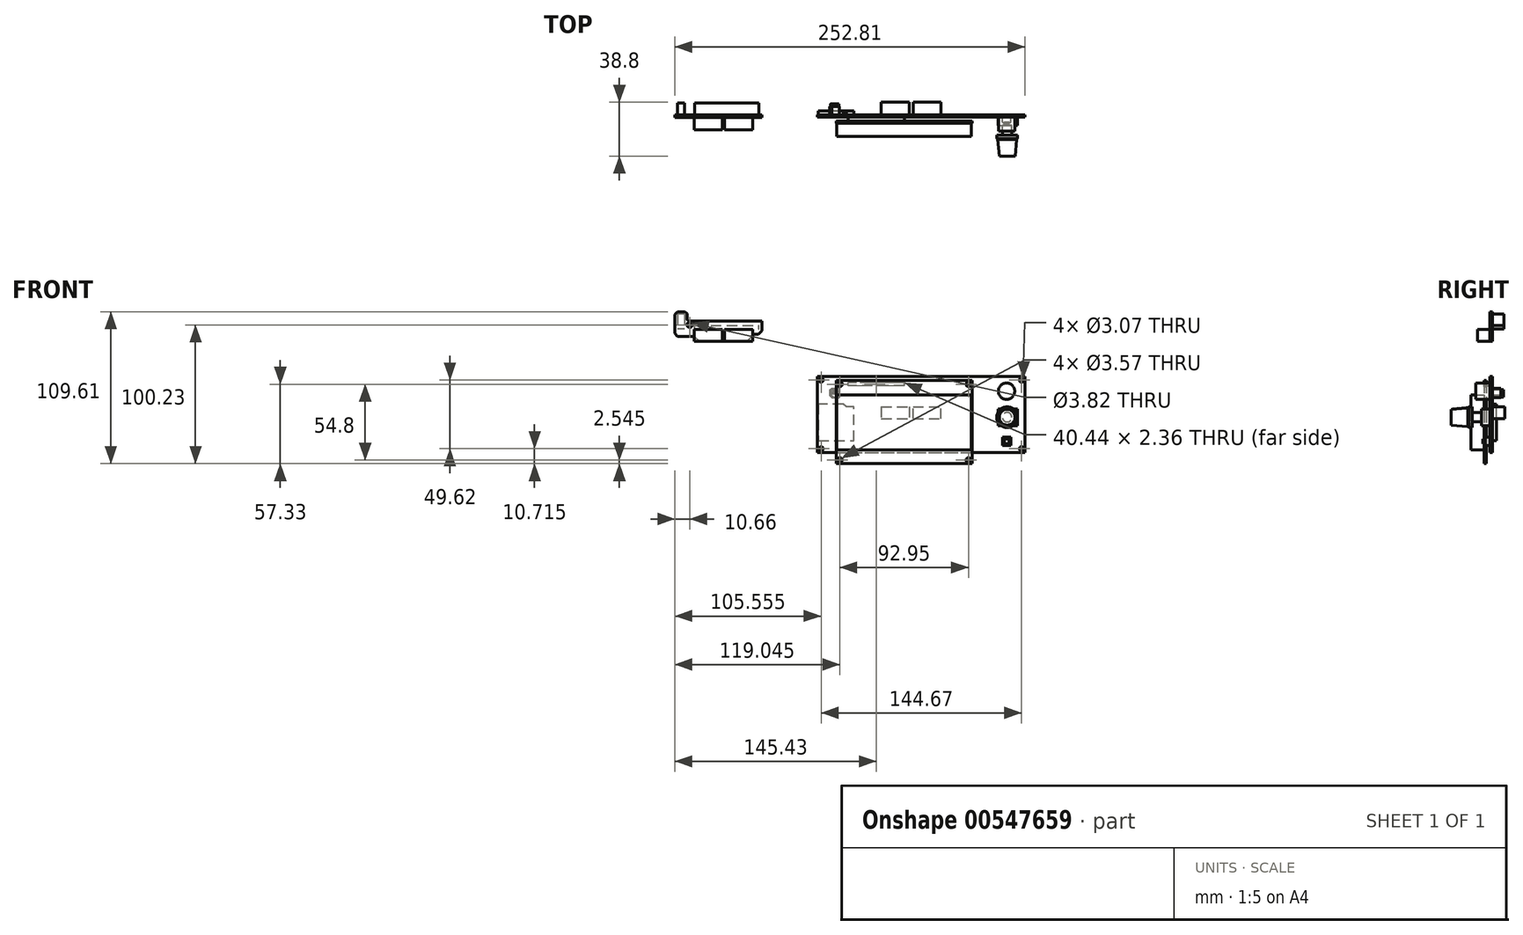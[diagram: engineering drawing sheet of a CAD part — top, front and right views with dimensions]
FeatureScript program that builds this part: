
annotation { "Feature Type Name" : "Feature", "Feature Type Description" : "" }
export const myFeature = defineFeature(function(context is Context, id is Id, definition is map)
    precondition{}
    {
        {
            var Q0;
            Q0=qCreatedBy(makeId("Front.planeOp"),FACE);
            var sketch = newSketch(context, id + "F0", { "sketchPlane" : qUnion([Q0])});
            skLineSegment(sketch, "E0.bottom", {"start": v(0, 0) * mm, "end": v(150.07, 0) * mm});
            skLineSegment(sketch, "E0.top", {"start": v(0, -55.1) * mm, "end": v(150.07, -55.1) * mm});
            skLineSegment(sketch, "E0.left", {"start": v(0, 0) * mm, "end": v(0, -55.1) * mm});
            skLineSegment(sketch, "E0.right", {"start": v(150.07, 0) * mm, "end": v(150.07, -55.1) * mm});
            skLineSegment(sketch, "E1", {"start": v(0, -2.7) * mm, "end": v(150.07, -2.7) * mm, "construction": true});
            skLineSegment(sketch, "E2", {"start": v(0, -52.33) * mm, "end": v(150.07, -52.32) * mm, "construction": true});
            skLineSegment(sketch, "E3", {"start": v(2.81, 0) * mm, "end": v(2.82, -55.1) * mm, "construction": true});
            skLineSegment(sketch, "E4", {"start": v(147.49, 0) * mm, "end": v(147.49, -55.1) * mm, "construction": true});
            skCircle(sketch, "E5", {"center": v(2.81, -2.7) * mm, "radius": 1.53 * mm});
            skCircle(sketch, "E6", {"center": v(2.81, -52.33) * mm, "radius": 1.53 * mm});
            skCircle(sketch, "E7", {"center": v(147.49, -2.7) * mm, "radius": 1.53 * mm});
            skCircle(sketch, "E8", {"center": v(147.49, -52.32) * mm, "radius": 1.53 * mm});
            skSolve(sketch);
        }
        {
            var Q0;
            Q0=qSketchRegion(id+"F0",true);
            extrude(context, id + "F1", {"entities" : qUnion([Q0]), "depth" : 1.63 * mm});
        }
        {
            var Q0;
            Q0=makeQuery(id+"F1.opExtrude","CAP_FACE",FACE,{"disambiguationData":[OSD([sQuery(id+"F0.wireOp",EDGE,"E0.bottom"),sQuery(id+"F0.wireOp",EDGE,"E0.top"),sQuery(id+"F0.wireOp",EDGE,"E0.left"),sQuery(id+"F0.wireOp",EDGE,"E0.right")])],"isStart":false});
            cPlane(context, id + "F2", {"entities" : qUnion([Q0]), "cplaneType" : CPlaneType.OFFSET, "offset" : 2.7 * mm, "width" : 150 * mm, "height" : 150 * mm});
        }
        {
            var Q0;
            Q0=qCreatedBy(id+"F2.planeOp",FACE);
            var sketch = newSketch(context, id + "F3", { "sketchPlane" : qUnion([Q0])});
            skLineSegment(sketch, "E9.bottom", {"start": v(13.62, -3.08) * mm, "end": v(111.77, -3.08) * mm});
            skLineSegment(sketch, "E9.top", {"start": v(13.62, -63.04) * mm, "end": v(111.77, -63.04) * mm});
            skLineSegment(sketch, "E9.left", {"start": v(13.62, -3.08) * mm, "end": v(13.62, -63.04) * mm});
            skLineSegment(sketch, "E9.right", {"start": v(111.77, -3.08) * mm, "end": v(111.77, -63.04) * mm});
            skLineSegment(sketch, "E10.bottom", {"start": v(16.3, -5.7) * mm, "end": v(109.26, -5.7) * mm, "construction": true});
            skLineSegment(sketch, "E10.top", {"start": v(16.3, -60.5) * mm, "end": v(109.26, -60.5) * mm, "construction": true});
            skLineSegment(sketch, "E10.left", {"start": v(16.3, -5.7) * mm, "end": v(16.3, -60.5) * mm, "construction": true});
            skLineSegment(sketch, "E10.right", {"start": v(109.26, -5.7) * mm, "end": v(109.26, -60.5) * mm, "construction": true});
            skCircle(sketch, "E11", {"center": v(16.3, -5.7) * mm, "radius": 1.78 * mm});
            skCircle(sketch, "E12", {"center": v(109.26, -5.7) * mm, "radius": 1.78 * mm});
            skCircle(sketch, "E13", {"center": v(16.3, -60.5) * mm, "radius": 1.78 * mm});
            skCircle(sketch, "E14", {"center": v(109.26, -60.5) * mm, "radius": 1.78 * mm});
            skSolve(sketch);
        }
        {
            var Q0;
            Q0=qSketchRegion(id+"F3",true);
            extrude(context, id + "F4", {"entities" : qUnion([Q0]), "depth" : 1.62 * mm});
        }
        {
            var Q0;
            Q0=makeQuery(id+"F4.opExtrude","CAP_FACE",FACE,{"disambiguationData":[OSD([sQuery(id+"F3.wireOp",EDGE,"E9.bottom"),sQuery(id+"F3.wireOp",EDGE,"E9.top"),sQuery(id+"F3.wireOp",EDGE,"E9.left"),sQuery(id+"F3.wireOp",EDGE,"E9.right")])],"isStart":false});
            var sketch = newSketch(context, id + "F5", { "sketchPlane" : qUnion([Q0])});
            skLineSegment(sketch, "E15", {"start": v(62.7, -3.08) * mm, "end": v(62.7, -63.04) * mm, "construction": true});
            skLineSegment(sketch, "E16.bottom", {"start": v(14.18, -13.36) * mm, "end": v(111.2, -13.36) * mm});
            skLineSegment(sketch, "E16.top", {"start": v(14.19, -53.18) * mm, "end": v(111.2, -53.18) * mm});
            skLineSegment(sketch, "E16.left", {"start": v(14.19, -13.36) * mm, "end": v(14.19, -53.18) * mm});
            skLineSegment(sketch, "E16.right", {"start": v(111.2, -13.36) * mm, "end": v(111.2, -53.18) * mm});
            skCircle(sketch, "E17", {"center": v(62.7, -33.06) * mm, "radius": 48.5 * mm, "construction": true});
            skSolve(sketch);
        }
        {
            var Q0;
            Q0=qSketchRegion(id+"F5",true);
            extrude(context, id + "F6", {"entities" : qUnion([Q0]), "operationType" : NewBodyOperationType.ADD, "depth" : 9.45 * mm});
        }
        {
            var Q0;
            Q0=makeQuery(id+"F1.opExtrude","CAP_FACE",FACE,{"disambiguationData":[OSD([sQuery(id+"F0.wireOp",EDGE,"E0.bottom"),sQuery(id+"F0.wireOp",EDGE,"E0.top"),sQuery(id+"F0.wireOp",EDGE,"E0.left"),sQuery(id+"F0.wireOp",EDGE,"E0.right")])],"isStart":false});
            var sketch = newSketch(context, id + "F7", { "sketchPlane" : qUnion([Q0])});
            skLineSegment(sketch, "E18.bottom", {"start": v(133.8, -43.96) * mm, "end": v(139.76, -43.96) * mm});
            skLineSegment(sketch, "E18.top", {"start": v(133.8, -49.92) * mm, "end": v(139.76, -49.92) * mm});
            skLineSegment(sketch, "E18.left", {"start": v(133.8, -43.96) * mm, "end": v(133.8, -49.92) * mm});
            skLineSegment(sketch, "E18.right", {"start": v(139.76, -43.96) * mm, "end": v(139.76, -49.92) * mm});
            skCircle(sketch, "E19", {"center": v(136.78, -46.94) * mm, "radius": 2.98 * mm, "construction": true});
            skSolve(sketch);
        }
        {
            var Q0;
            Q0=qSketchRegion(id+"F7",true);
            extrude(context, id + "F8", {"entities" : qUnion([Q0]), "operationType" : NewBodyOperationType.ADD, "depth" : 3.55 * mm});
        }
        {
            var Q0;
            Q0=makeQuery(id+"F8.opExtrude","CAP_FACE",FACE,{"disambiguationData":[OSD([sQuery(id+"F7.wireOp",EDGE,"E18.bottom"),sQuery(id+"F7.wireOp",EDGE,"E18.top"),sQuery(id+"F7.wireOp",EDGE,"E18.left"),sQuery(id+"F7.wireOp",EDGE,"E18.right")])],"isStart":false});
            var sketch = newSketch(context, id + "F9", { "sketchPlane" : qUnion([Q0])});
            skLineSegment(sketch, "E20", {"start": v(133.8, -43.96) * mm, "end": v(139.76, -49.92) * mm, "construction": true});
            skCircle(sketch, "E21", {"center": v(136.78, -46.94) * mm, "radius": 1.76 * mm});
            skSolve(sketch);
        }
        {
            var Q0;
            Q0=qSketchRegion(id+"F9",true);
            extrude(context, id + "F10", {"entities" : qUnion([Q0]), "operationType" : NewBodyOperationType.ADD, "depth" : 1.57 * mm});
        }
        {
            var Q0;
            Q0=makeQuery(id+"F1.opExtrude","CAP_FACE",FACE,{"disambiguationData":[OSD([sQuery(id+"F0.wireOp",EDGE,"E0.bottom"),sQuery(id+"F0.wireOp",EDGE,"E0.top"),sQuery(id+"F0.wireOp",EDGE,"E0.left"),sQuery(id+"F0.wireOp",EDGE,"E0.right"),sQuery(id+"F0.wireOp",EDGE,"E5"),sQuery(id+"F0.wireOp",EDGE,"E6"),sQuery(id+"F0.wireOp",EDGE,"E7"),sQuery(id+"F0.wireOp",EDGE,"E8")])],"isStart":false});
            var sketch = newSketch(context, id + "F11", { "sketchPlane" : qUnion([Q0])});
            skLineSegment(sketch, "E22.bottom", {"start": v(130.73, -23.6) * mm, "end": v(144.54, -23.6) * mm});
            skLineSegment(sketch, "E22.top", {"start": v(130.73, -35.51) * mm, "end": v(144.54, -35.51) * mm});
            skLineSegment(sketch, "E22.left", {"start": v(130.73, -23.6) * mm, "end": v(130.73, -35.51) * mm});
            skLineSegment(sketch, "E22.right", {"start": v(144.54, -23.6) * mm, "end": v(144.54, -35.51) * mm});
            skSolve(sketch);
        }
        {
            var Q0;
            Q0=qSketchRegion(id+"F11",true);
            extrude(context, id + "F12", {"entities" : qUnion([Q0]), "operationType" : NewBodyOperationType.ADD, "depth" : 6.04 * mm});
        }
        {
            var Q0;
            Q0=makeQuery(id+"F12.opExtrude","CAP_FACE",FACE,{"disambiguationData":[OSD([sQuery(id+"F11.wireOp",EDGE,"E22.bottom"),sQuery(id+"F11.wireOp",EDGE,"E22.top"),sQuery(id+"F11.wireOp",EDGE,"E22.left"),sQuery(id+"F11.wireOp",EDGE,"E22.right")])],"isStart":false});
            var sketch = newSketch(context, id + "F13", { "sketchPlane" : qUnion([Q0])});
            skLineSegment(sketch, "E23", {"start": v(130.73, -29.55) * mm, "end": v(144.54, -29.55) * mm, "construction": true});
            skCircle(sketch, "E24", {"center": v(137.11, -29.55) * mm, "radius": 3.41 * mm});
            skSolve(sketch);
        }
        {
            var Q0;
            Q0=qSketchRegion(id+"F13",true);
            extrude(context, id + "F14", {"entities" : qUnion([Q0]), "operationType" : NewBodyOperationType.ADD, "depth" : 6.86 * mm});
        }
        {
            var Q0;
            Q0=sQuery(id+"F13.wireOp",EDGE,"E23");
            cPoint(context, id + "F15", {"entities" : qUnion([Q0]), "parameter" : 0.5});
        }
        {
            var Q0;
            Q0=qCreatedBy(makeId("Top.planeOp"),FACE);
            var Q1;
            Q1=qCreatedBy(id+"F15",VERTEX);
            cPlane(context, id + "F16", {"entities" : qUnion([Q0, Q1]), "cplaneType" : CPlaneType.PLANE_POINT, "offset" : 25 * mm, "width" : 150 * mm, "height" : 150 * mm});
        }
        {
            var Q0;
            Q0=qCreatedBy(id+"F16.planeOp",FACE);
            var sketch = newSketch(context, id + "F17", { "sketchPlane" : qUnion([Q0])});
            skLineSegment(sketch, "E25.0", {"start": v(140.52, -14.53) * mm, "end": v(133.7, -14.53) * mm, "construction": true});
            skLineSegment(sketch, "E26", {"start": v(137.11, -14.53) * mm, "end": v(137.11, -29.65) * mm});
            skLineSegment(sketch, "E27", {"start": v(137.11, -29.65) * mm, "end": v(142.84, -29.65) * mm});
            skLineSegment(sketch, "E28", {"start": v(142.84, -29.65) * mm, "end": v(143.96, -17.58) * mm});
            skLineSegment(sketch, "E29", {"start": v(143.96, -17.58) * mm, "end": v(144.6, -16.95) * mm});
            skLineSegment(sketch, "E30", {"start": v(144.6, -16.95) * mm, "end": v(144.6, -14.53) * mm});
            skLineSegment(sketch, "E31", {"start": v(144.6, -14.53) * mm, "end": v(137.11, -14.53) * mm});
            skSolve(sketch);
        }
        {
            var Q0;
            Q0=qSketchRegion(id+"F17",true);
            var Q1;
            Q1=sQuery(id+"F17.wireOp",EDGE,"E26");
            revolve(context, id + "F18", {"operationType" : NewBodyOperationType.ADD, "entities" : qUnion([Q0]), "axis" : qUnion([Q1]), "revolveType" : RevolveType.FULL});
        }
        {
            var Q0;
            Q0=makeQuery(id+"F1.opExtrude","CAP_FACE",FACE,{"disambiguationData":[OSD([sQuery(id+"F0.wireOp",EDGE,"E0.bottom"),sQuery(id+"F0.wireOp",EDGE,"E0.top"),sQuery(id+"F0.wireOp",EDGE,"E0.left"),sQuery(id+"F0.wireOp",EDGE,"E0.right"),sQuery(id+"F0.wireOp",EDGE,"E5"),sQuery(id+"F0.wireOp",EDGE,"E6"),sQuery(id+"F0.wireOp",EDGE,"E7"),sQuery(id+"F0.wireOp",EDGE,"E8")])],"isStart":false});
            var sketch = newSketch(context, id + "F19", { "sketchPlane" : qUnion([Q0])});
            skCircle(sketch, "E32", {"center": v(136.68, -10.73) * mm, "radius": 5.9 * mm});
            skSolve(sketch);
        }
        {
            var Q0;
            Q0=qSketchRegion(id+"F19",true);
            extrude(context, id + "F20", {"entities" : qUnion([Q0]), "operationType" : NewBodyOperationType.ADD, "depth" : 10.15 * mm});
        }
        {
            var Q0;
            Q0=makeQuery(id+"F1.opExtrude","CAP_FACE",FACE,{"disambiguationData":[OSD([sQuery(id+"F0.wireOp",EDGE,"E0.bottom"),sQuery(id+"F0.wireOp",EDGE,"E0.top"),sQuery(id+"F0.wireOp",EDGE,"E0.left"),sQuery(id+"F0.wireOp",EDGE,"E0.right"),sQuery(id+"F0.wireOp",EDGE,"E5"),sQuery(id+"F0.wireOp",EDGE,"E6"),sQuery(id+"F0.wireOp",EDGE,"E7"),sQuery(id+"F0.wireOp",EDGE,"E8")])],"isStart":true});
            var sketch = newSketch(context, id + "F21", { "sketchPlane" : qUnion([Q0])});
            skLineSegment(sketch, "E33", {"start": v(-0.8, -46.57) * mm, "end": v(-26.48, -46.57) * mm});
            skLineSegment(sketch, "E34", {"start": v(-26.48, -46.57) * mm, "end": v(-26.48, -22.15) * mm});
            skLineSegment(sketch, "E35", {"start": v(-26.48, -22.15) * mm, "end": v(-21.02, -22.15) * mm});
            skLineSegment(sketch, "E36", {"start": v(-21.02, -22.15) * mm, "end": v(-18.87, -20) * mm});
            skLineSegment(sketch, "E37", {"start": v(-18.87, -20) * mm, "end": v(-0.8, -20) * mm});
            skLineSegment(sketch, "E38", {"start": v(-0.8, -20) * mm, "end": v(-0.8, -46.57) * mm});
            skSolve(sketch);
        }
        {
            var Q0;
            Q0=qSketchRegion(id+"F21",true);
            extrude(context, id + "F22", {"entities" : qUnion([Q0]), "operationType" : NewBodyOperationType.ADD, "depth" : 2.91 * mm});
        }
        {
            var Q0;
            Q0=makeQuery(id+"F1.opExtrude","CAP_FACE",FACE,{"disambiguationData":[OSD([sQuery(id+"F0.wireOp",EDGE,"E0.bottom"),sQuery(id+"F0.wireOp",EDGE,"E0.top"),sQuery(id+"F0.wireOp",EDGE,"E0.left"),sQuery(id+"F0.wireOp",EDGE,"E0.right"),sQuery(id+"F0.wireOp",EDGE,"E5"),sQuery(id+"F0.wireOp",EDGE,"E6"),sQuery(id+"F0.wireOp",EDGE,"E7"),sQuery(id+"F0.wireOp",EDGE,"E8")])],"isStart":true});
            var sketch = newSketch(context, id + "F23", { "sketchPlane" : qUnion([Q0])});
            skLineSegment(sketch, "E39", {"start": v(-15.96, -11.92) * mm, "end": v(-9.02, -11.92) * mm, "construction": true});
            skLineSegment(sketch, "E40", {"start": v(-9.02, -11.92) * mm, "end": v(-9.02, -10.05) * mm});
            skLineSegment(sketch, "E41", {"start": v(-9.02, -10.05) * mm, "end": v(-10.48, -8.6) * mm});
            skLineSegment(sketch, "E42", {"start": v(-10.48, -8.6) * mm, "end": v(-15.96, -8.6) * mm});
            skLineSegment(sketch, "E43", {"start": v(-15.96, -8.6) * mm, "end": v(-15.96, -11.92) * mm});
            skLineSegment(sketch, "E44.MirrorCS", {"start": v(-15.96, -15.25) * mm, "end": v(-15.96, -11.92) * mm});
            skLineSegment(sketch, "E45.MirrorCS", {"start": v(-10.48, -15.25) * mm, "end": v(-15.96, -15.25) * mm});
            skLineSegment(sketch, "E46.MirrorCS", {"start": v(-9.02, -13.78) * mm, "end": v(-10.49, -15.25) * mm});
            skLineSegment(sketch, "E47.MirrorCS", {"start": v(-9.02, -11.92) * mm, "end": v(-9.02, -13.78) * mm});
            skSolve(sketch);
        }
        {
            var Q0;
            Q0=qSketchRegion(id+"F23",true);
            extrude(context, id + "F24", {"entities" : qUnion([Q0]), "operationType" : NewBodyOperationType.ADD, "depth" : 6.15 * mm});
        }
        {
            var Q0;
            Q0=makeQuery(id+"F24.opExtrude","CAP_FACE",FACE,{"disambiguationData":[OSD([sQuery(id+"F23.wireOp",EDGE,"E40"),sQuery(id+"F23.wireOp",EDGE,"E41"),sQuery(id+"F23.wireOp",EDGE,"E42"),sQuery(id+"F23.wireOp",EDGE,"E43"),sQuery(id+"F23.wireOp",EDGE,"E44.MirrorCS"),sQuery(id+"F23.wireOp",EDGE,"E45.MirrorCS"),sQuery(id+"F23.wireOp",EDGE,"E46.MirrorCS"),sQuery(id+"F23.wireOp",EDGE,"E47.MirrorCS")])],"isStart":false});
            var sketch = newSketch(context, id + "F25", { "sketchPlane" : qUnion([Q0])});
            skLineSegment(sketch, "E48.0", {"start": v(-15.96, -11.92) * mm, "end": v(-9.02, -11.92) * mm, "construction": true});
            skCircle(sketch, "E49", {"center": v(-12.5, -11.92) * mm, "radius": 3 * mm});
            skLineSegment(sketch, "E50.bottom", {"start": v(-14.72, -11.4) * mm, "end": v(-12.5, -11.4) * mm});
            skLineSegment(sketch, "E50.left", {"start": v(-14.72, -11.4) * mm, "end": v(-14.72, -11.92) * mm});
            skLineSegment(sketch, "E51", {"start": v(-12.5, -11.92) * mm, "end": v(-12.5, -8.91) * mm, "construction": true});
            skLineSegment(sketch, "E52", {"start": v(-12.5, -11.92) * mm, "end": v(-12.5, -14.93) * mm, "construction": true});
            skLineSegment(sketch, "E53", {"start": v(-14.25, -9.48) * mm, "end": v(-13.82, -9.48) * mm});
            skLineSegment(sketch, "E54", {"start": v(-13.82, -9.48) * mm, "end": v(-13.82, -10.03) * mm});
            skLineSegment(sketch, "E55", {"start": v(-13.82, -10.03) * mm, "end": v(-12.5, -10.03) * mm});
            skLineSegment(sketch, "E56.MirrorCS", {"start": v(-14.72, -12.45) * mm, "end": v(-12.5, -12.45) * mm});
            skLineSegment(sketch, "E57.MirrorCS", {"start": v(-14.72, -12.45) * mm, "end": v(-14.72, -11.92) * mm});
            skLineSegment(sketch, "E58.MirrorCS", {"start": v(-11.16, -10.03) * mm, "end": v(-12.5, -10.03) * mm});
            skLineSegment(sketch, "E59.MirrorCS", {"start": v(-11.16, -9.48) * mm, "end": v(-11.16, -10.03) * mm});
            skLineSegment(sketch, "E60.MirrorCS", {"start": v(-10.73, -9.48) * mm, "end": v(-11.16, -9.48) * mm});
            skLineSegment(sketch, "E61.MirrorCS", {"start": v(-10.27, -11.4) * mm, "end": v(-12.5, -11.4) * mm});
            skLineSegment(sketch, "E62.MirrorCS", {"start": v(-10.27, -11.4) * mm, "end": v(-10.27, -11.92) * mm});
            skLineSegment(sketch, "E63.MirrorCS", {"start": v(-10.27, -12.45) * mm, "end": v(-10.27, -11.92) * mm});
            skLineSegment(sketch, "E64.MirrorCS", {"start": v(-10.27, -12.45) * mm, "end": v(-12.5, -12.45) * mm});
            skSolve(sketch);
        }
        {
            var Q0;
            Q0=makeQuery(id+"F25.imprint","IMPRINT",FACE,{"disambiguationData":[TD([[makeQuery(id+"F25.imprint","IMPRINT",EDGE,{"derivedFrom":sQuery(id+"F25.wireOp",EDGE,"E50.bottom")}),1.0]])]});
            extrude(context, id + "F26", {"entities" : qUnion([Q0]), "operationType" : NewBodyOperationType.ADD, "depth" : 1.85 * mm});
        }
        {
            var Q0;
            Q0=makeQuery(id+"F1.opExtrude","CAP_FACE",FACE,{"disambiguationData":[OSD([sQuery(id+"F0.wireOp",EDGE,"E0.bottom"),sQuery(id+"F0.wireOp",EDGE,"E0.top"),sQuery(id+"F0.wireOp",EDGE,"E0.left"),sQuery(id+"F0.wireOp",EDGE,"E0.right"),sQuery(id+"F0.wireOp",EDGE,"E5"),sQuery(id+"F0.wireOp",EDGE,"E6"),sQuery(id+"F0.wireOp",EDGE,"E7"),sQuery(id+"F0.wireOp",EDGE,"E8")])],"isStart":true});
            var sketch = newSketch(context, id + "F27", { "sketchPlane" : qUnion([Q0])});
            skLineSegment(sketch, "E65.bottom", {"start": v(-46.17, -22) * mm, "end": v(-66.44, -22) * mm});
            skLineSegment(sketch, "E65.top", {"start": v(-46.17, -30.71) * mm, "end": v(-66.44, -30.71) * mm});
            skLineSegment(sketch, "E65.left", {"start": v(-46.17, -22) * mm, "end": v(-46.17, -30.71) * mm});
            skLineSegment(sketch, "E65.right", {"start": v(-66.44, -22) * mm, "end": v(-66.44, -30.71) * mm});
            skLineSegment(sketch, "E66.bottom", {"start": v(-69.19, -30.71) * mm, "end": v(-89.46, -30.71) * mm});
            skLineSegment(sketch, "E66.top", {"start": v(-69.19, -22) * mm, "end": v(-89.46, -22) * mm});
            skLineSegment(sketch, "E66.left", {"start": v(-69.19, -30.71) * mm, "end": v(-69.19, -22) * mm});
            skLineSegment(sketch, "E66.right", {"start": v(-89.46, -30.71) * mm, "end": v(-89.46, -22) * mm});
            skLineSegment(sketch, "E67", {"start": v(-69.19, -30.71) * mm, "end": v(-66.44, -30.71) * mm, "construction": true});
            skLineSegment(sketch, "E68", {"start": v(-66.44, -22) * mm, "end": v(-69.19, -22) * mm, "construction": true});
            skSolve(sketch);
        }
        {
            var Q0;
            Q0=qSketchRegion(id+"F27",true);
            extrude(context, id + "F28", {"entities" : qUnion([Q0]), "operationType" : NewBodyOperationType.ADD, "depth" : 9.15 * mm});
        }
        {
            var Q0;
            Q0=qCreatedBy(makeId("Front.planeOp"),FACE);
            var sketch = newSketch(context, id + "F29", { "sketchPlane" : qUnion([Q0])});
            skLineSegment(sketch, "E69", {"start": v(-40, 40) * mm, "end": v(-92.4, 40) * mm});
            skLineSegment(sketch, "E70", {"start": v(-93.99, 41.6) * mm, "end": v(-93.99, 45.24) * mm});
            skLineSegment(sketch, "E71", {"start": v(-93.99, 45.24) * mm, "end": v(-95.32, 46.57) * mm});
            skLineSegment(sketch, "E72", {"start": v(-95.32, 46.57) * mm, "end": v(-100.78, 46.57) * mm});
            skLineSegment(sketch, "E73", {"start": v(-100.78, 46.57) * mm, "end": v(-102.74, 44.6) * mm});
            skLineSegment(sketch, "E74", {"start": v(-102.74, 44.6) * mm, "end": v(-102.74, 30.85) * mm});
            skLineSegment(sketch, "E75", {"start": v(-102.74, 30.85) * mm, "end": v(-100.78, 28.89) * mm});
            skLineSegment(sketch, "E76", {"start": v(-100.78, 28.89) * mm, "end": v(-88.78, 28.89) * mm});
            skLineSegment(sketch, "E77", {"start": v(-88.78, 28.89) * mm, "end": v(-85.05, 25.16) * mm});
            skLineSegment(sketch, "E78", {"start": v(-85.05, 25.16) * mm, "end": v(-50.73, 25.16) * mm});
            skLineSegment(sketch, "E79", {"start": v(-50.73, 25.16) * mm, "end": v(-45.51, 30.38) * mm});
            skLineSegment(sketch, "E80", {"start": v(-42.42, 30.38) * mm, "end": v(-40, 32.8) * mm});
            skLineSegment(sketch, "E81", {"start": v(-40, 32.8) * mm, "end": v(-40, 40) * mm});
            skLineSegment(sketch, "E82", {"start": v(-45.51, 30.38) * mm, "end": v(-42.42, 30.38) * mm});
            skLineSegment(sketch, "E83", {"start": v(-100.78, 46.57) * mm, "end": v(-100.78, 28.89) * mm, "construction": true});
            skPoint(sketch, "E84.visualSharp", {"position": v(-93.99, 40) * mm});
            skArc(sketch, "E84.filletArc", {"start": v(-94, 41.6) * mm, "mid": v(-93.52, 40.47) * mm, "end": v(-92.4, 40) * mm});
            skCircle(sketch, "E85", {"center": v(-92.08, 37.19) * mm, "radius": 1.91 * mm});
            skLineSegment(sketch, "E86", {"start": v(-93.99, 41.6) * mm, "end": v(-93.99, 28.89) * mm, "construction": true});
            skSolve(sketch);
        }
        {
            var Q0;
            Q0=qSketchRegion(id+"F29",true);
            extrude(context, id + "F30", {"entities" : qUnion([Q0]), "depth" : 1.74 * mm});
        }
        {
            var Q0;
            Q0=makeQuery(id+"F30.opExtrude","CAP_FACE",FACE,{"disambiguationData":[OSD([sQuery(id+"F29.wireOp",EDGE,"E69"),sQuery(id+"F29.wireOp",EDGE,"E70"),sQuery(id+"F29.wireOp",EDGE,"E71"),sQuery(id+"F29.wireOp",EDGE,"E72"),sQuery(id+"F29.wireOp",EDGE,"E73"),sQuery(id+"F29.wireOp",EDGE,"E74"),sQuery(id+"F29.wireOp",EDGE,"E75"),sQuery(id+"F29.wireOp",EDGE,"E76"),sQuery(id+"F29.wireOp",EDGE,"E77"),sQuery(id+"F29.wireOp",EDGE,"E78"),sQuery(id+"F29.wireOp",EDGE,"E79"),sQuery(id+"F29.wireOp",EDGE,"E80"),sQuery(id+"F29.wireOp",EDGE,"E81"),sQuery(id+"F29.wireOp",EDGE,"E82"),sQuery(id+"F29.wireOp",EDGE,"E84.filletArc"),sQuery(id+"F29.wireOp",EDGE,"E85")])],"isStart":false});
            var sketch = newSketch(context, id + "F31", { "sketchPlane" : qUnion([Q0])});
            skLineSegment(sketch, "E87.bottom", {"start": v(-68.54, 25.16) * mm, "end": v(-88.78, 25.16) * mm});
            skLineSegment(sketch, "E87.top", {"start": v(-68.54, 33.78) * mm, "end": v(-88.78, 33.78) * mm});
            skLineSegment(sketch, "E87.left", {"start": v(-68.54, 25.16) * mm, "end": v(-68.54, 33.78) * mm});
            skLineSegment(sketch, "E87.right", {"start": v(-88.78, 25.16) * mm, "end": v(-88.78, 33.78) * mm});
            skLineSegment(sketch, "E88.bottom", {"start": v(-66.85, 25.16) * mm, "end": v(-46.58, 25.16) * mm});
            skLineSegment(sketch, "E88.top", {"start": v(-66.85, 33.78) * mm, "end": v(-46.58, 33.78) * mm});
            skLineSegment(sketch, "E88.left", {"start": v(-66.85, 25.16) * mm, "end": v(-66.85, 33.78) * mm});
            skLineSegment(sketch, "E88.right", {"start": v(-46.58, 25.16) * mm, "end": v(-46.58, 33.78) * mm});
            skLineSegment(sketch, "E89", {"start": v(-68.54, 33.78) * mm, "end": v(-66.85, 33.78) * mm, "construction": true});
            skSolve(sketch);
        }
        {
            var Q0;
            Q0=qSketchRegion(id+"F31",true);
            extrude(context, id + "F32", {"entities" : qUnion([Q0]), "operationType" : NewBodyOperationType.ADD, "depth" : 9.02 * mm});
        }
        {
            var Q0;
            Q0=makeQuery(id+"F30.opExtrude","CAP_FACE",FACE,{"disambiguationData":[OSD([sQuery(id+"F29.wireOp",EDGE,"E69"),sQuery(id+"F29.wireOp",EDGE,"E70"),sQuery(id+"F29.wireOp",EDGE,"E71"),sQuery(id+"F29.wireOp",EDGE,"E72"),sQuery(id+"F29.wireOp",EDGE,"E73"),sQuery(id+"F29.wireOp",EDGE,"E74"),sQuery(id+"F29.wireOp",EDGE,"E75"),sQuery(id+"F29.wireOp",EDGE,"E76"),sQuery(id+"F29.wireOp",EDGE,"E77"),sQuery(id+"F29.wireOp",EDGE,"E78"),sQuery(id+"F29.wireOp",EDGE,"E79"),sQuery(id+"F29.wireOp",EDGE,"E80"),sQuery(id+"F29.wireOp",EDGE,"E81"),sQuery(id+"F29.wireOp",EDGE,"E82"),sQuery(id+"F29.wireOp",EDGE,"E84.filletArc"),sQuery(id+"F29.wireOp",EDGE,"E85")])],"isStart":true});
            var sketch = newSketch(context, id + "F33", { "sketchPlane" : qUnion([Q0])});
            skLineSegment(sketch, "E90.bottom", {"start": v(95.85, 44.89) * mm, "end": v(100.83, 44.89) * mm});
            skLineSegment(sketch, "E90.top", {"start": v(95.85, 34.32) * mm, "end": v(100.83, 34.32) * mm});
            skLineSegment(sketch, "E90.left", {"start": v(95.85, 44.89) * mm, "end": v(95.85, 34.32) * mm});
            skLineSegment(sketch, "E90.right", {"start": v(100.83, 44.89) * mm, "end": v(100.83, 34.32) * mm});
            skLineSegment(sketch, "E91.bottom", {"start": v(88.33, 34.32) * mm, "end": v(42.1, 34.32) * mm});
            skLineSegment(sketch, "E91.top", {"start": v(88.33, 36.69) * mm, "end": v(42.1, 36.69) * mm});
            skLineSegment(sketch, "E91.left", {"start": v(88.33, 34.32) * mm, "end": v(88.33, 36.69) * mm});
            skLineSegment(sketch, "E91.right", {"start": v(42.1, 34.32) * mm, "end": v(42.1, 36.69) * mm});
            skLineSegment(sketch, "E92", {"start": v(88.33, 34.32) * mm, "end": v(95.85, 34.32) * mm, "construction": true});
            skSolve(sketch);
        }
        {
            var Q0;
            Q0=qSketchRegion(id+"F33",true);
            extrude(context, id + "F34", {"entities" : qUnion([Q0]), "operationType" : NewBodyOperationType.ADD, "depth" : 8.52 * mm});
        }
        {
            var Q0;
            Q0=makeQuery(id+"F1.opExtrude","CAP_FACE",FACE,{"disambiguationData":[OSD([sQuery(id+"F0.wireOp",EDGE,"E0.bottom"),sQuery(id+"F0.wireOp",EDGE,"E0.top"),sQuery(id+"F0.wireOp",EDGE,"E0.left"),sQuery(id+"F0.wireOp",EDGE,"E0.right"),sQuery(id+"F0.wireOp",EDGE,"E5"),sQuery(id+"F0.wireOp",EDGE,"E6"),sQuery(id+"F0.wireOp",EDGE,"E7"),sQuery(id+"F0.wireOp",EDGE,"E8")])],"isStart":true});
            var sketch = newSketch(context, id + "F35", { "sketchPlane" : qUnion([Q0])});
            skLineSegment(sketch, "E93.bottom", {"start": v(-22.47, -4.53) * mm, "end": v(-62.9, -4.53) * mm});
            skLineSegment(sketch, "E93.top", {"start": v(-22.47, -6.9) * mm, "end": v(-62.9, -6.9) * mm});
            skLineSegment(sketch, "E93.left", {"start": v(-22.47, -4.53) * mm, "end": v(-22.47, -6.9) * mm});
            skLineSegment(sketch, "E93.right", {"start": v(-62.9, -4.53) * mm, "end": v(-62.9, -6.9) * mm});
            skSolve(sketch);
        }
        {
            var Q0;
            Q0=qSketchRegion(id+"F35",true);
            var Q1;
            Q1=makeQuery(id+"F4.opExtrude","CAP_FACE",FACE,{"disambiguationData":[OSD([sQuery(id+"F3.wireOp",EDGE,"E9.bottom"),sQuery(id+"F3.wireOp",EDGE,"E9.top"),sQuery(id+"F3.wireOp",EDGE,"E9.left"),sQuery(id+"F3.wireOp",EDGE,"E9.right"),sQuery(id+"F3.wireOp",EDGE,"E11"),sQuery(id+"F3.wireOp",EDGE,"E12"),sQuery(id+"F3.wireOp",EDGE,"E13"),sQuery(id+"F3.wireOp",EDGE,"E14")])],"isStart":true});
            extrude(context, id + "F36", {"entities" : qUnion([Q0]), "operationType" : NewBodyOperationType.ADD, "endBound" : BoundingType.UP_TO_SURFACE, "oppositeDirection" : true, "endBoundEntityFace" : qUnion([Q1]), "depth" : 25 * mm});
        }
    });
